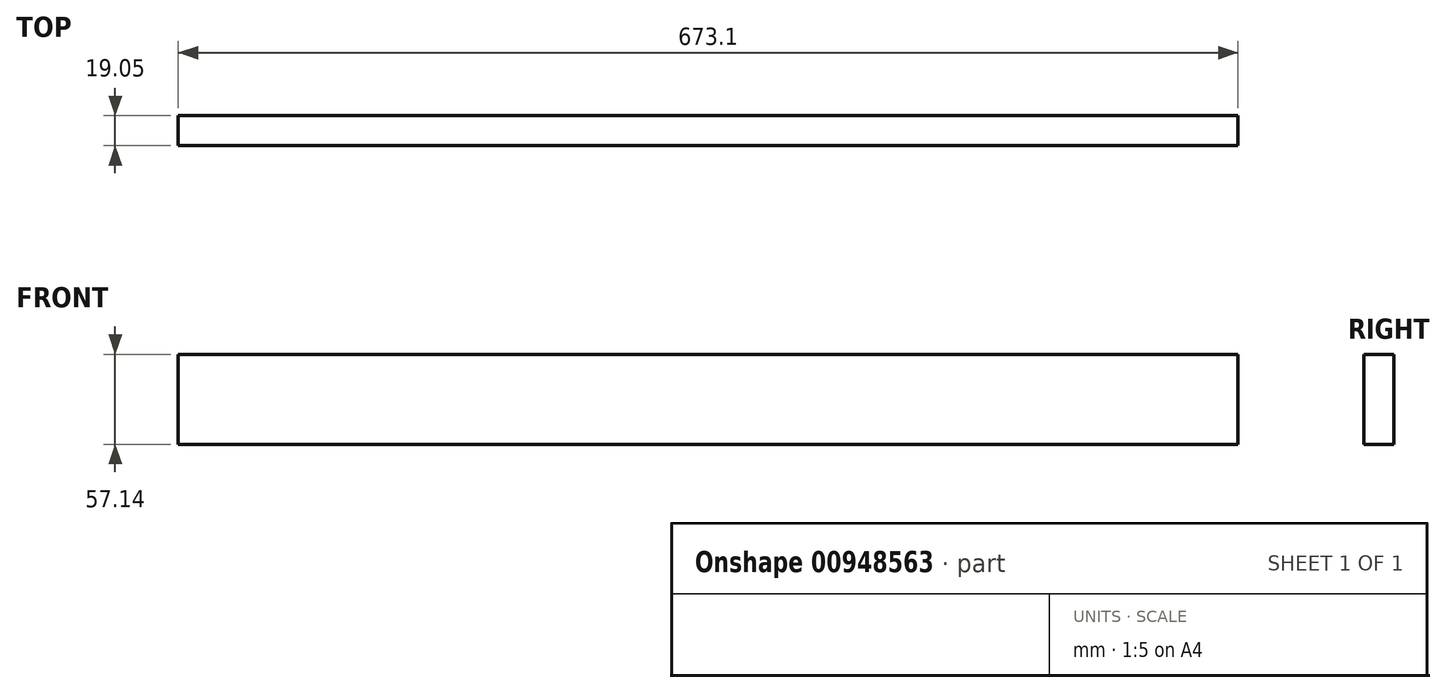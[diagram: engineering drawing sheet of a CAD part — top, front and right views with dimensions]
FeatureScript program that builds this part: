
annotation { "Feature Type Name" : "Feature", "Feature Type Description" : "" }
export const myFeature = defineFeature(function(context is Context, id is Id, definition is map)
    precondition{}
    {
        {
            var Q0;
            Q0=qCreatedBy(makeId("Front.planeOp"),FACE);
            var sketch = newSketch(context, id + "F0", { "sketchPlane" : qUnion([Q0])});
            skLineSegment(sketch, "E0.bottom", {"start": v(336.55, -28.57) * mm, "end": v(-336.55, -28.58) * mm});
            skLineSegment(sketch, "E0.top", {"start": v(336.55, 28.58) * mm, "end": v(-336.55, 28.58) * mm});
            skLineSegment(sketch, "E0.left", {"start": v(336.55, -28.57) * mm, "end": v(336.55, 28.58) * mm});
            skLineSegment(sketch, "E0.right", {"start": v(-336.55, -28.58) * mm, "end": v(-336.55, 28.58) * mm});
            skPoint(sketch, "E0.middle", {"position": v(0, 0) * mm});
            skSolve(sketch);
        }
        {
            var Q0;
            Q0=makeQuery(id+"F0.imprint","IMPRINT",FACE,{"disambiguationData":[TD([[makeQuery(id+"F0.imprint","IMPRINT",EDGE,{"derivedFrom":sQuery(id+"F0.wireOp",EDGE,"E0.bottom")}),-1.0]])]});
            extrude(context, id + "F1", {"entities" : qUnion([Q0]), "depth" : 19.05 * mm, "offsetDistance" : 25.4 * mm});
        }
    });
